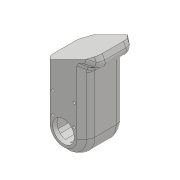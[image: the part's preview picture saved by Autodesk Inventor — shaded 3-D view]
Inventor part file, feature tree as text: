
AUTODESK INVENTOR PART (.ipt)
format: ipt  version: 2018 (Build 220112000, 112)  size: 652,800 bytes
history: native  units: mm
features: sketch x26, extrude x23, projected_geometry x22, fillet x5, hole x3, chamfer x3, mirror x1, plane x1
ambient origin geometry x8: Origin, YZ Plane, XZ Plane, XY Plane, X Axis, Y Axis, Z Axis, Center Point
bodies: Solid1 (feature_tree)
feature tree (84):
  extrude  "Extrusion1"  Depth=45.0mm
  extrude  "Extrusion2"  Depth=1.95mm
  hole  "Hole1"  [1 undecoded]
  hole  "Hole2"  [1 undecoded]
  fillet  "Fillet1"  Radius=14.0mm
  extrude  "Extrusion3"  Depth=18.5mm
  extrude  "Extrusion4"  Depth=20.5mm
  extrude  "Extrusion5"  Depth=2.195mm
  extrude  "Extrusion6"  Depth=20.5mm
  hole  "Hole3"  [1 undecoded]
  extrude  "Extrusion7"  Depth=0.5mm
  extrude  "Extrusion8"  Depth=5.0mm TaperAngle=0.0deg
  extrude  "Extrusion9"  Depth=24.5mm
  extrude  "Extrusion10"  Depth=10.0mm
  extrude  "Extrusion11"  Depth=14.5mm
  extrude  "Extrusion12"  Depth=14.5mm
  extrude  "Extrusion13"  Depth=5.0mm
  extrude  "Extrusion14"  Depth=2.25mm
  extrude  "Extrusion15"  Depth=5.0mm
  extrude  "Extrusion16"  Depth=9.0mm
  extrude  "Extrusion17"  Depth=4.0mm
  chamfer  "Chamfer1"  Distance=1.0mm
  fillet  "Fillet7"  Radius=20.7mm
  fillet  "Fillet8"  Radius=32.0mm
  mirror  "Mirror1"
  extrude  "Extrusion24"  Depth=1.0mm TaperAngle=0.0deg
  extrude  "Extrusion25"  Depth=8.0mm
  extrude  "Extrusion26"  Depth=0.2mm TaperAngle=0.0deg
  extrude  "Extrusion27"  Depth=21.0mm
  extrude  "Extrusion28"  Depth=0.5mm TaperAngle=0.0deg
  chamfer  "Chamfer5"  Distance=8.0mm
  fillet  "Fillet18"  Radius=5.0mm
  fillet  "Fillet19"  Radius=5.0mm
  extrude  "Extrusion29"  Depth=0.2mm TaperAngle=0.0deg
  chamfer  "Chamfer6"  Distance=0.2mm
  plane  "Work Plane2"
  sketch  "Sketch1"  dims[d0=24.5mm d1=45.0mm]
  sketch  "Sketch2"  dims[d2=1.95mm d3=0.0mm d4=2.25mm]
  projected_geometry  "Projected Loop1"
  sketch  "Sketch3"  dims[d5=20.0mm d6=2.25mm]
  projected_geometry  "Projected Loop2"
  sketch  "Sketch4"  dims[d7=5.25mm d8=5.25mm d9=14.0mm]
  projected_geometry  "Projected Loop3"
  sketch  "Sketch5"  dims[d10=5.25mm d11=18.5mm]
  projected_geometry  "Projected Loop4"
  sketch  "Sketch6"  dims[d12=10.0mm d13=0.0mm d14=20.5mm]
  projected_geometry  "Projected Loop5"
  sketch  "Sketch7"  dims[d15=2.0mm d16=2.195mm]
  projected_geometry  "Projected Loop6"
  sketch  "Sketch8"  dims[d17=2.0mm]
  projected_geometry  "Projected Loop7"
  sketch  "Sketch9"  dims[d18=2.4mm d19=6.0mm d20=4.4mm d21=2.0mm d22=90.0deg d23=8.0mm d24=20.594885mm d25=20.5mm]
  projected_geometry  "Projected Loop8"
  projected_geometry  "Projected Loop9"
  sketch  "Sketch10"  dims[d26=26.65mm d27=2.0mm]
  projected_geometry  "Projected Loop10"
  projected_geometry  "Projected Loop11"
  sketch  "Sketch11"  dims[d28=2.0mm]
  projected_geometry  "Projected Loop12"
  sketch  "Sketch12"  dims[d29=2.4mm d30=6.0mm d31=4.4mm d32=2.0mm d33=90.0deg d34=8.0mm d35=20.594885mm d36=0.5mm]
  sketch  "Sketch13"  dims[d37=18.0mm d38=5.0mm d39=0.0mm]
  sketch  "Sketch14"  dims[d41=10.0mm d42=0.0mm d43=24.5mm]
  projected_geometry  "Projected Loop13"
  sketch  "Sketch15"  dims[d44=1.15mm d45=0.0mm d46=10.0mm]
  sketch  "Sketch16"  dims[d47=21.0mm d48=14.5mm]
  projected_geometry  "Projected Loop14"
  sketch  "Sketch17"  dims[d49=20.0mm d50=14.5mm]
  projected_geometry  "Projected Loop15"
  sketch  "Sketch18"  dims[d51=24.5mm d52=5.0mm]
  projected_geometry  "Projected Loop16"
  sketch  "Sketch19"  dims[d53=5.0mm d54=2.25mm]
  projected_geometry  "Projected Loop17"
  sketch  "Sketch20"  dims[d55=2.25mm d56=5.0mm]
  projected_geometry  "Projected Loop18"
  sketch  "Sketch35"  dims[d57=5.0mm d58=9.0mm]
  projected_geometry  "Projected Loop28"
  sketch  "Sketch36"  dims[d59=14.75mm d60=4.0mm d61=1.0mm d62=0.0mm d63=20.7mm]
  projected_geometry  "Projected Loop29"
  sketch  "Sketch37"  dims[d64=2.4mm d65=6.0mm d66=4.4mm d67=2.0mm d68=90.0deg d69=8.0mm d70=20.594885mm d72=32.0mm]
  sketch  "Sketch38"  dims[d73=5.0mm d74=0.0mm d75=1.0mm d76=0.0mm]
  sketch  "Sketch39"  dims[d77=12.25mm d78=0.0mm d80=8.0mm]
  projected_geometry  "Projected Loop30"
  sketch  "Sketch40"  dims[d81=4.5mm d82=0.0mm d84=0.2mm d85=0.0mm d86=21.0mm d87=0.5mm d88=0.0mm d91=8.0mm d92=0.0mm d93=5.0mm d94=0.0mm d95=5.0mm d96=0.0mm d98=0.2mm d99=0.0mm d100=0.2mm d101=0.0mm d102=2.5mm d103=2.0mm d104=45.0deg d105=1.5mm d114=0.5mm d187=40.0mm d188=70.0mm d189=20.0mm d190=10.0mm d191=0.0mm d192=10.0mm d193=0.0mm d194=2.0mm d195=0.0mm d196=2.0mm d197=0.0mm d198=8.0mm d199=10.0mm d200=2.0mm d201=0.0mm d204=7.0mm d205=2.0mm d206=45.0deg d207=5.0mm d208=8.0mm d209=15.0mm d210=2.0mm d211=0.0mm d212=1.5mm d213=2.0mm d214=45.0deg]
  projected_geometry  "Projected Loop31"
note: 3 required parameter values undecoded (feature->parameter linkage not recoverable at this tier; creation-order binding heuristic only, values carry confidence <= 0.55)
